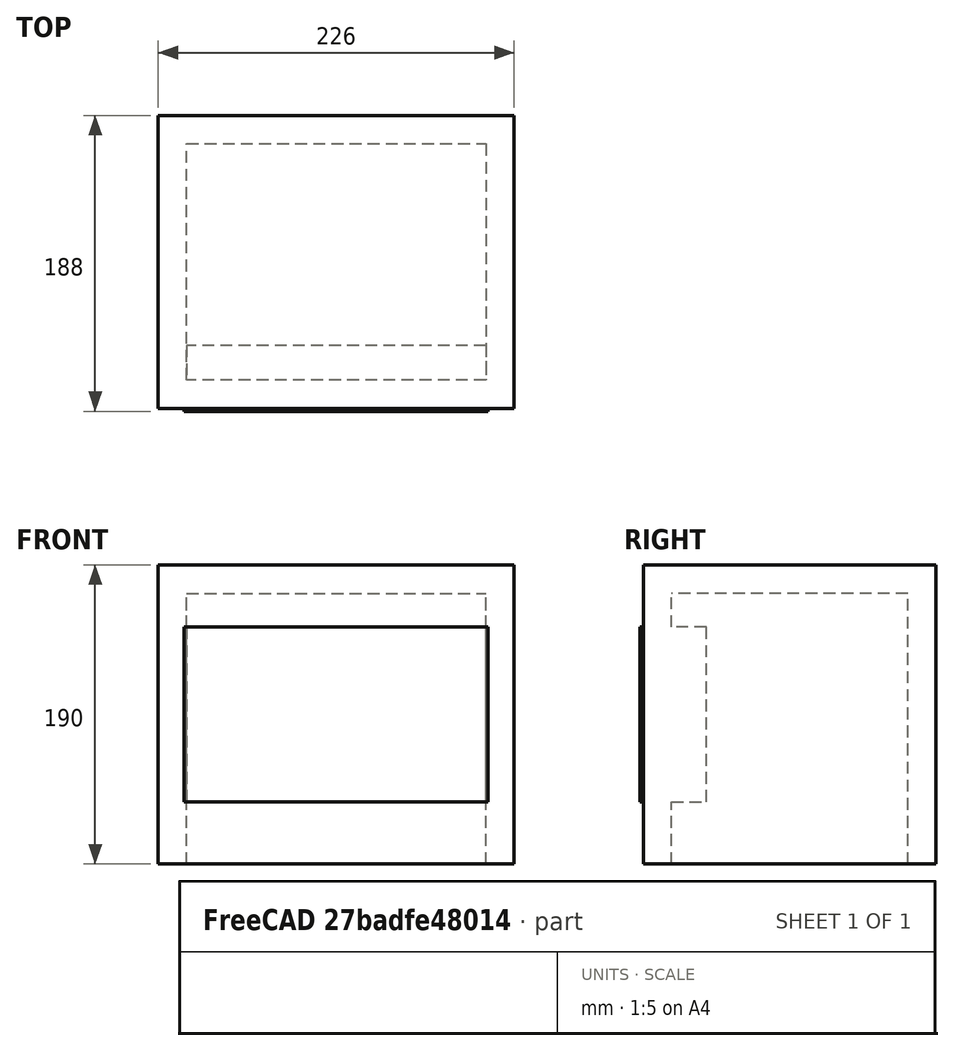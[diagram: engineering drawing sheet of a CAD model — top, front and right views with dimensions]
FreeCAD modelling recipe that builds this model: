
FCSTD DOCUMENT  (FreeCAD 0.18.4R)
Label: Behuizing
License: All rights reserved
LicenseURL: http://en.wikipedia.org/wiki/All_rights_reserved
objects: Sketcher::SketchObject×4, PartDesign::Pad×4, TechDraw::DrawViewDimension×4, TechDraw::DrawViewPart×3, PartDesign::LinearPattern×2, TechDraw::DrawSVGTemplate×1, PartDesign::Body×1, TechDraw::DrawPage×1
note: 15 computed .brp shape members not serialized (recipe doc carries the construction recipe); baked Part::Feature solids carry a one-line shape summary decoded from their .brp

FEATURE [Sketcher::SketchObject] Sketch  label="Sketch voorkant"
  MapMode = 5
  Support = -> [XY_Plane]
  expr: Constraints[9] = 240 - 14
  sketch-geometry (4):
    g0: LineSegment StartX=0 StartY=0 StartZ=0 EndX=226 EndY=0 EndZ=0
    g1: LineSegment StartX=226 StartY=0 StartZ=0 EndX=226 EndY=18 EndZ=0
    g2: LineSegment StartX=226 StartY=18 StartZ=0 EndX=0 EndY=18 EndZ=0
    g3: LineSegment StartX=0 StartY=18 StartZ=0 EndX=0 EndY=0 EndZ=0
  constraints (11):
    c: Coincident(g0,g1)
    c: Coincident(g1,g2)
    c: Coincident(g2,g3)
    c: Coincident(g3,g0)
    c: Horizontal(g0)
    c: Horizontal(g2)
    c: Vertical(g1)
    c: Vertical(g3)
    c: Coincident(g0,g-1)
    c: Distance(g2) = 226
    c: Distance(g3) = 18
FEATURE [PartDesign::Pad] Pad  label="Voorkant"
  Length = 190
  Length2 = 100
  Profile = -> Sketch
  Type = 0
FEATURE [Sketcher::SketchObject] Sketch001  label="Sketch zijkant links"
  ExternalGeometry = -> [Pad]
  MapMode = 5
  Support = -> [XY_Plane]
  sketch-geometry (4):
    g0: LineSegment StartX=0 StartY=18 StartZ=0 EndX=18 EndY=18 EndZ=0
    g1: LineSegment StartX=18 StartY=18 StartZ=0 EndX=18 EndY=168 EndZ=0
    g2: LineSegment StartX=18 StartY=168 StartZ=0 EndX=0 EndY=168 EndZ=0
    g3: LineSegment StartX=0 StartY=168 StartZ=0 EndX=0 EndY=18 EndZ=0
  constraints (11):
    c: Coincident(g0,g1)
    c: Coincident(g1,g2)
    c: Coincident(g2,g3)
    c: Coincident(g3,g0)
    c: Horizontal(g2)
    c: Vertical(g1)
    c: Vertical(g3)
    c: PointOnObject(g0,g-2)
    c: Distance(g3) = 150
    c: Distance(g2) = 18
    c: Tangent(g0,g-3)
FEATURE [PartDesign::Pad] Pad001  label="Zijkant links"
  BaseFeature = -> Pad
  Length = 190
  Length2 = 100
  Profile = -> Sketch001
  Type = 0
FEATURE [PartDesign::LinearPattern] LinearPattern  label="Achterkant"
  BaseFeature = -> Pad001
  Direction = -> Pad001 [Edge17]
  Length = 168
  Occurrences = 2
  Originals = -> [Pad]
  Reversed = true
FEATURE [PartDesign::LinearPattern] LinearPattern001  label="Zijkant rechts"
  BaseFeature = -> LinearPattern
  Direction = -> X_Axis
  Length = 208
  Occurrences = 2
  Originals = -> [Pad001]
  expr: Length = 240 - 14 - 18
FEATURE [Sketcher::SketchObject] Sketch002
  AttachmentOffset = pos=(0,0,172) rot=(0,0,1;0rad)
  ExternalGeometry = -> [LinearPattern001]
  MapMode = 5
  Placement = pos=(0,0,172) rot=(0,0,1;0rad)
  Support = -> [XY_Plane]
  expr: AttachmentOffset.Base.z = 190 - 18
  sketch-geometry (4):
    g0: LineSegment StartX=18 StartY=168 StartZ=0 EndX=208 EndY=168 EndZ=0
    g1: LineSegment StartX=208 StartY=168 StartZ=0 EndX=208 EndY=18 EndZ=0
    g2: LineSegment StartX=208 StartY=18 StartZ=0 EndX=18 EndY=18 EndZ=0
    g3: LineSegment StartX=18 StartY=18 StartZ=0 EndX=18 EndY=168 EndZ=0
  constraints (8):
    c: Coincident(g0,g1)
    c: Coincident(g1,g2)
    c: Coincident(g2,g3)
    c: Coincident(g3,g0)
    c: Tangent(g1,g-6)
    c: Tangent(g2,g-5)
    c: Tangent(g3,g-4)
    c: Tangent(g0,g-3)
FEATURE [PartDesign::Pad] Pad002  label="Bovenkant"
  BaseFeature = -> LinearPattern001
  Length = 18
  Length2 = 100
  Profile = -> Sketch002
  Type = 0
FEATURE [TechDraw::DrawSVGTemplate] Template
  EditableTexts = AUTHOR_NAME=Jens Willemsens; DN=DN; DRAWING_TITLE=SUNRISE ALARM; FC-DATE=17/08/2020; FC-REV=REV A; FC-SC=0.5; FC-SH=X / Y; FC-SI=A3; PN=PN
  Height = 297
  Orientation = 1
  Width = 420
FEATURE [Sketcher::SketchObject] Sketch003
  AttachmentOffset = pos=(0,0,-40) rot=(0,0,1;0rad)
  ExternalGeometry = -> [Pad002]
  MapMode = 5
  Placement = pos=(0,40,-8.9e-15) rot=(1,0,0;1.5708rad)
  Support = -> [XZ_Plane]
  expr: Constraints[11] = (190 - 111) / 2
  expr: Constraints[10] = (226 - 193) / 2
  sketch-geometry (5):
    g0: LineSegment StartX=16.5 StartY=150.5 StartZ=0 EndX=209.5 EndY=150.5 EndZ=0
    g1: LineSegment StartX=209.5 StartY=150.5 StartZ=0 EndX=209.5 EndY=39.5 EndZ=0
    g2: LineSegment StartX=209.5 StartY=39.5 StartZ=0 EndX=16.5 EndY=39.5 EndZ=0
    g3: LineSegment StartX=16.5 StartY=39.5 StartZ=0 EndX=16.5 EndY=150.5 EndZ=0
    g4: GeomPoint X=120 Y=95 Z=0
  constraints (12):
    c: Coincident(g0,g1)
    c: Coincident(g1,g2)
    c: Coincident(g2,g3)
    c: Coincident(g3,g0)
    c: Horizontal(g0)
    c: Vertical(g1)
    c: Distance(g0) = 193
    c: Distance(g1) = 111
    c: Horizontal(g2)
    c: Vertical(g3)
    c: DistanceX(g-1,g2) = 16.5
    c: DistanceY(g0,g-6) = 39.5
FEATURE [PartDesign::Pad] Pad003  label="Scherm"
  BaseFeature = -> Pad002
  Length = 42
  Length2 = 100
  Profile = -> Sketch003
  Type = 0
FEATURE [PartDesign::Body] Body  label="Behuizing"
  Group = -> [Sketch,Pad,Sketch001,Pad001,LinearPattern,LinearPattern001,Sketch002,Pad002,Sketch003,Pad003]
  Origin = -> Origin
  Tip = -> Pad003
FEATURE [TechDraw::DrawViewPart] View  label="Perspectief"
  CoarseView = false
  Direction = (-0.565,-0.673,0.476)
  Focus = 100
  HardHidden = false
  IsoCount = 0
  IsoHidden = false
  IsoVisible = false
  LockPosition = false
  Perspective = false
  Rotation = 0
  Scale = 0.5
  ScaleType = 0
  SeamHidden = false
  SeamVisible = false
  SmoothHidden = false
  SmoothVisible = false
  Source = -> [Body]
  X = 300.781
  Y = 182.496
FEATURE [TechDraw::DrawViewPart] View001  label="Top"
  CoarseView = false
  Direction = (0,0,-1)
  Focus = 100
  HardHidden = false
  IsoCount = 0
  IsoHidden = false
  IsoVisible = false
  LockPosition = false
  Perspective = false
  Rotation = 180
  Scale = 0.5
  ScaleType = 0
  SeamHidden = false
  SeamVisible = false
  SmoothHidden = false
  SmoothVisible = false
  Source = -> [Body]
  X = 120.34
  Y = 89.1
FEATURE [TechDraw::DrawViewPart] View002  label="Front"
  CoarseView = false
  Direction = (0,-1,0)
  Focus = 100
  HardHidden = false
  IsoCount = 0
  IsoHidden = false
  IsoVisible = false
  LockPosition = false
  Perspective = false
  Rotation = 0
  Scale = 0.5
  ScaleType = 0
  SeamHidden = false
  SeamVisible = false
  SmoothHidden = false
  SmoothVisible = false
  Source = -> [Body]
  X = 119.219
  Y = 217.24
FEATURE [TechDraw::DrawViewDimension] Dimension
  Arbitrary = false
  FormatSpec = %.2f
  LockPosition = false
  MeasureType = 1
  OverTolerance = 0
  References2D = -> [View002]
  Rotation = 0
  ScaleType = 0
  Type = 0
  UnderTolerance = 0
  X = -3.41035
  Y = 60.4593
FEATURE [TechDraw::DrawViewDimension] Dimension001
  Arbitrary = false
  FormatSpec = %.2f
  LockPosition = false
  MeasureType = 1
  OverTolerance = 0
  References2D = -> [View002]
  Rotation = 0
  ScaleType = 0
  Type = 0
  UnderTolerance = 0
  X = -72.5286
  Y = 1.70517
FEATURE [TechDraw::DrawViewDimension] Dimension002
  Arbitrary = false
  FormatSpec = %.2f
  LockPosition = false
  MeasureType = 1
  OverTolerance = 0
  References2D = -> [View001]
  Rotation = 0
  ScaleType = 0
  Type = 0
  UnderTolerance = 0
  X = 0.341035
  Y = 58.8031
FEATURE [TechDraw::DrawViewDimension] Dimension003
  Arbitrary = false
  FormatSpec = %.2f
  LockPosition = false
  MeasureType = 1
  OverTolerance = 0
  References2D = -> [View001]
  Rotation = 0
  ScaleType = 0
  Type = 0
  UnderTolerance = 0
  X = -74.1007
  Y = -1.88724
FEATURE [TechDraw::DrawPage] Page
  KeepUpdated = true
  ProjectionType = 0
  Template = -> Template
  Views = -> [View,View001,View002,Dimension,Dimension001,Dimension002,Dimension003]
